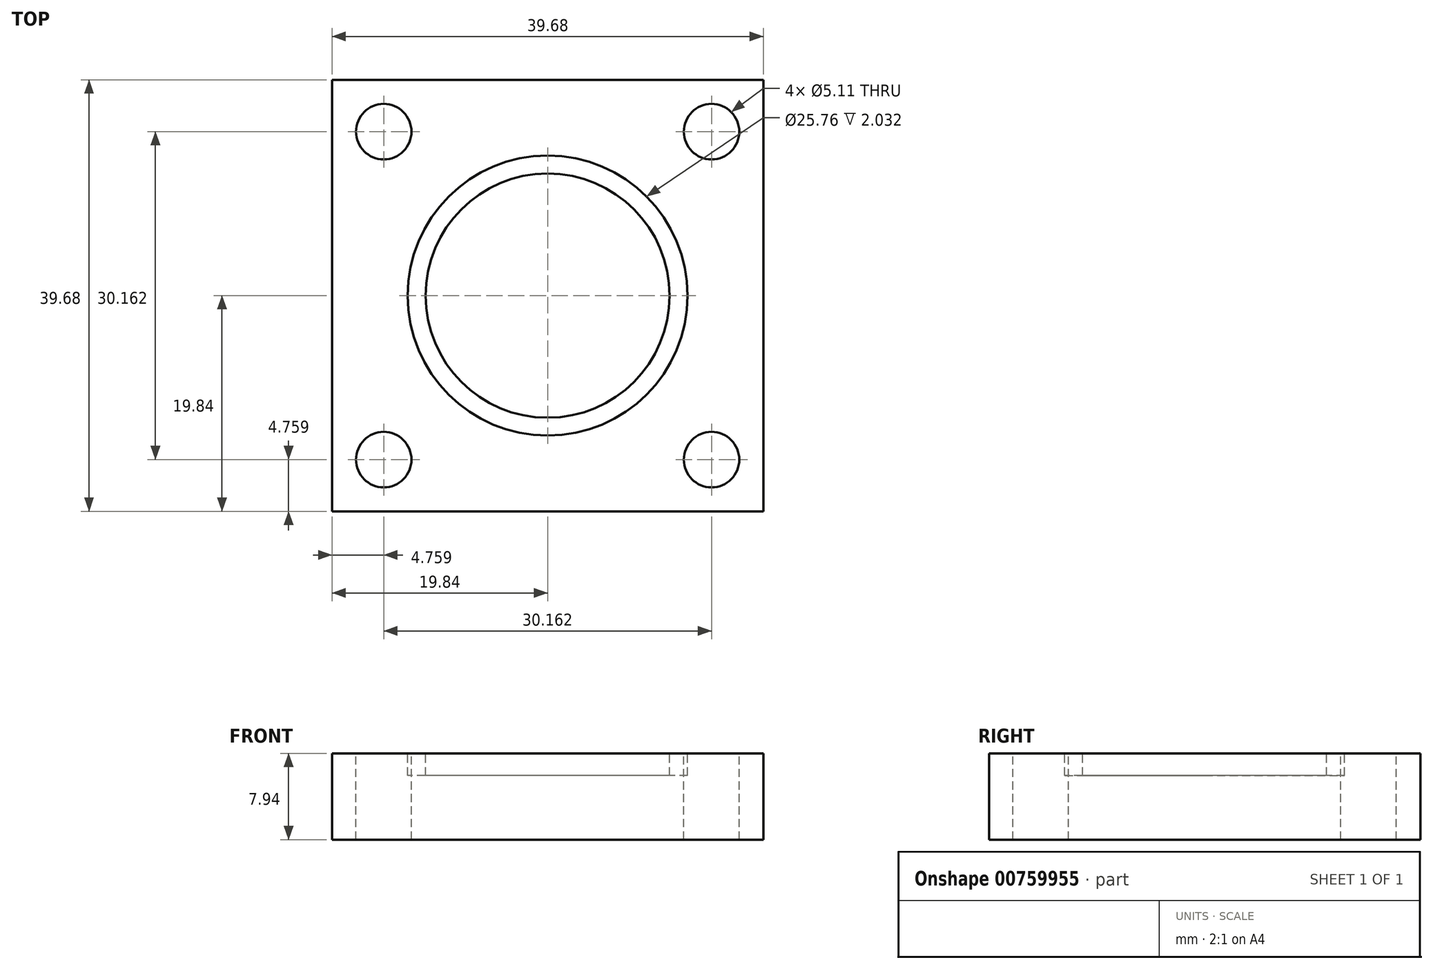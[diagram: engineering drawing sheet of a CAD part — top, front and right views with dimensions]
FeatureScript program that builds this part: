
annotation { "Feature Type Name" : "Feature", "Feature Type Description" : "" }
export const myFeature = defineFeature(function(context is Context, id is Id, definition is map)
    precondition{}
    {
        {
            var Q0;
            Q0=qCreatedBy(makeId("Top.planeOp"),FACE);
            var sketch = newSketch(context, id + "F0", { "sketchPlane" : qUnion([Q0])});
            skLineSegment(sketch, "E0.bottom", {"start": v(19.84, -19.84) * mm, "end": v(-19.84, -19.84) * mm});
            skLineSegment(sketch, "E0.top", {"start": v(19.84, 19.84) * mm, "end": v(-19.84, 19.84) * mm});
            skLineSegment(sketch, "E0.left", {"start": v(19.84, -19.84) * mm, "end": v(19.84, 19.84) * mm});
            skLineSegment(sketch, "E0.right", {"start": v(-19.84, -19.84) * mm, "end": v(-19.84, 19.84) * mm});
            skPoint(sketch, "E0.middle", {"position": v(0, 0) * mm});
            skCircle(sketch, "E1", {"center": v(0, 0) * mm, "radius": 12.88 * mm});
            skCircle(sketch, "E2", {"center": v(0, 0) * mm, "radius": 11.23 * mm});
            skPoint(sketch, "E3", {"position": v(-15.08, 15.08) * mm});
            skPoint(sketch, "E4.MirrorP", {"position": v(15.08, 15.08) * mm});
            skPoint(sketch, "E5.MirrorP", {"position": v(-15.08, -15.08) * mm});
            skPoint(sketch, "E6.MirrorP", {"position": v(15.08, -15.08) * mm});
            skSolve(sketch);
        }
        {
            var Q0;
            Q0=makeQuery(id+"F0.imprint","IMPRINT",FACE,{"disambiguationData":[TD([[makeQuery(id+"F0.imprint","IMPRINT",EDGE,{"derivedFrom":sQuery(id+"F0.wireOp",EDGE,"E0.bottom")}),-1.0]])]});
            var Q1;
            Q1=makeQuery(id+"F0.imprint","IMPRINT",FACE,{"disambiguationData":[TD([[makeQuery(id+"F0.imprint","IMPRINT",EDGE,{"derivedFrom":sQuery(id+"F0.wireOp",EDGE,"E1")}),1.0]])]});
            var Q2;
            Q2=makeQuery(id+"F0.imprint","IMPRINT",FACE,{"disambiguationData":[TD([[makeQuery(id+"F0.imprint","IMPRINT",EDGE,{"derivedFrom":sQuery(id+"F0.wireOp",EDGE,"E2")}),1.0]])]});
            extrude(context, id + "F1", {"entities" : qUnion([Q0, Q1, Q2]), "oppositeDirection" : true, "depth" : 7.94 * mm, "offsetDistance" : 25.4 * mm});
        }
        {
            var Q0;
            Q0=makeQuery(id+"F0.imprint","IMPRINT",FACE,{"disambiguationData":[TD([[makeQuery(id+"F0.imprint","IMPRINT",EDGE,{"derivedFrom":sQuery(id+"F0.wireOp",EDGE,"E1")}),1.0]])]});
            extrude(context, id + "F2", {"entities" : qUnion([Q0]), "operationType" : NewBodyOperationType.REMOVE, "oppositeDirection" : true, "depth" : 2.03 * mm, "offsetDistance" : 25.4 * mm});
        }
        {
            var Q0;
            Q0=sQuery(id+"F0.wireOp",VERTEX,"E3");
            var Q1;
            Q1=sQuery(id+"F0.wireOp",VERTEX,"E4.MirrorP");
            var Q2;
            Q2=sQuery(id+"F0.wireOp",VERTEX,"E6.MirrorP");
            var Q3;
            Q3=sQuery(id+"F0.wireOp",VERTEX,"E5.MirrorP");
            var Q4;
            Q4=makeQuery(id+"F1.opExtrude","SWEPT_BODY",BODY,{"disambiguationData":[OSD([sQuery(id+"F0.wireOp",EDGE,"E0.bottom"),sQuery(id+"F0.wireOp",EDGE,"E0.top"),sQuery(id+"F0.wireOp",EDGE,"E0.left"),sQuery(id+"F0.wireOp",EDGE,"E0.right")])]});
            hole(context, id + "F3", {"style" : HoleStyle.SIMPLE, "endStyle" : HoleEndStyle.THROUGH, "standardTappedOrClearance" : lookupTablePath({ "standard" : "ANSI", "fit" : "Normal (ASME)", "size" : "#10", "type" : "Clearance" }), "standardBlindInLast" : lookupTablePath({ "fit" : "Free", "standard" : "ANSI", "size" : "#10", "type" : "Clearance" }), "holeDiameter" : 5.1 * mm, "majorDiameter" : 6.35 * mm, "isTappedThrough" : true, "tappedDepth" : 12.7 * mm, "tapClearance" : 3, "locations" : qUnion([Q0, Q1, Q2, Q3]), "scope" : qUnion([Q4])});
        }
    });
